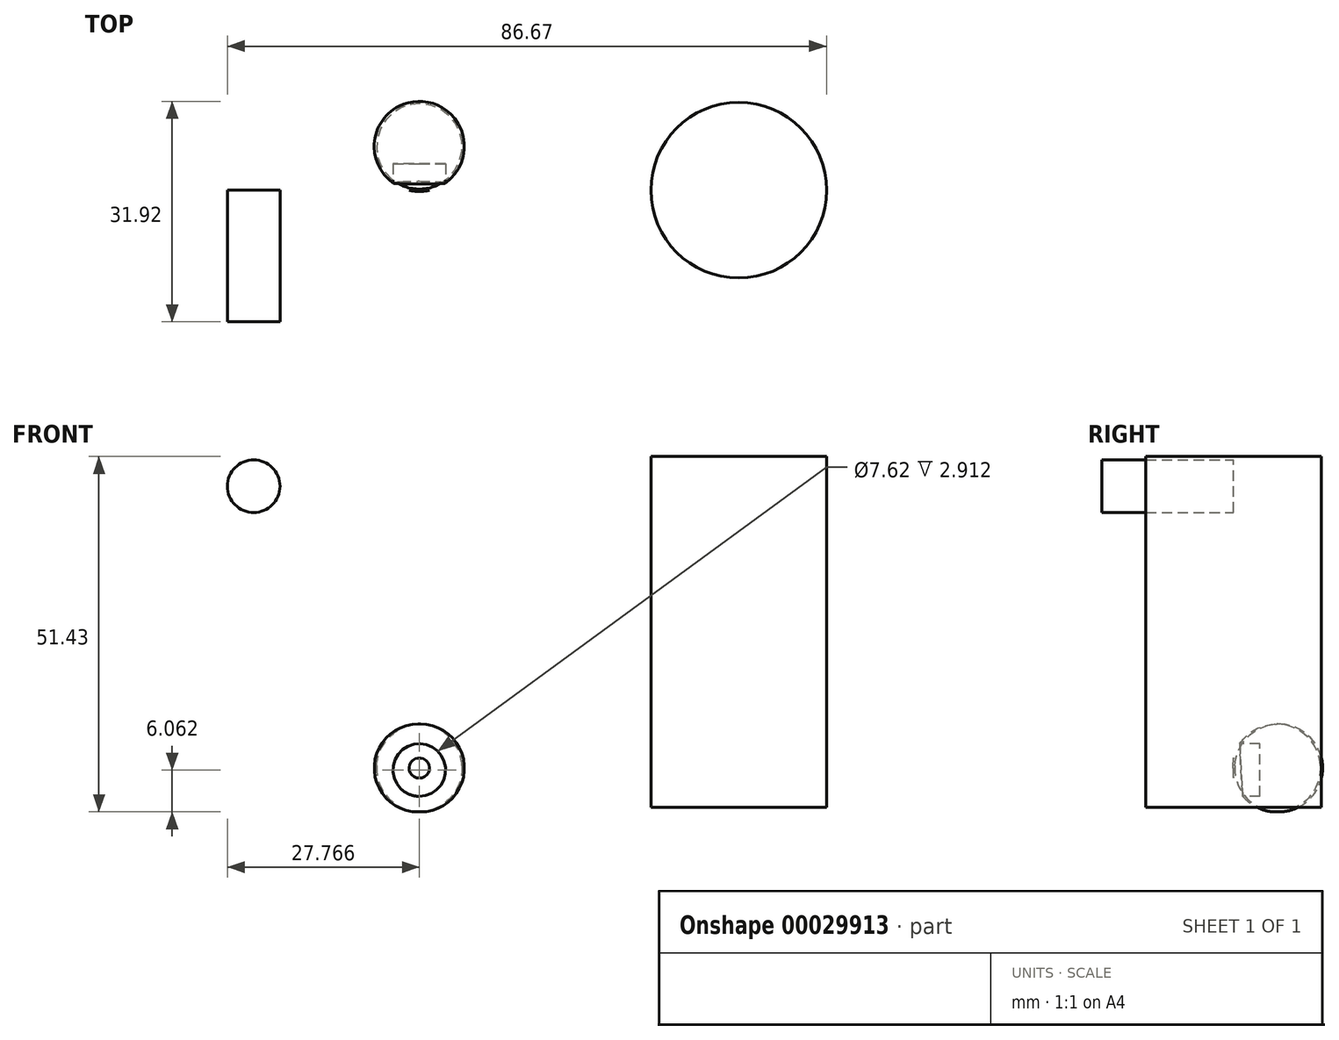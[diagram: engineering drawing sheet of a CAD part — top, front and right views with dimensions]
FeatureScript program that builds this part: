
annotation { "Feature Type Name" : "Feature", "Feature Type Description" : "" }
export const myFeature = defineFeature(function(context is Context, id is Id, definition is map)
    precondition{}
    {
        {
            var Q0;
            Q0=qCreatedBy(makeId("Front.planeOp"),FACE);
            var sketch = newSketch(context, id + "F0", { "sketchPlane" : qUnion([Q0])});
            skLineSegment(sketch, "E0", {"start": v(-25.81, -11.2) * mm, "end": v(-25.81, -23.9) * mm});
            skArc(sketch, "E1", {"start": v(-25.81, -11.2) * mm, "mid": v(-32.33, -17.54) * mm, "end": v(-25.81, -23.9) * mm});
            skSolve(sketch);
        }
        {
            var Q0;
            Q0=makeQuery(id+"F0.imprint","IMPRINT",FACE,{"disambiguationData":[TD([[makeQuery(id+"F0.imprint","IMPRINT",EDGE,{"derivedFrom":sQuery(id+"F0.wireOp",EDGE,"E0")}),-1.0]])]});
            var Q1;
            Q1=sQuery(id+"F0.wireOp",EDGE,"E0");
            revolve(context, id + "F1", {"entities" : qUnion([Q0]), "axis" : qUnion([Q1]), "revolveType" : RevolveType.FULL});
        }
        {
            var Q0;
            Q0=qCreatedBy(makeId("Front.planeOp"),FACE);
            cPlane(context, id + "F2", {"entities" : qUnion([Q0]), "cplaneType" : CPlaneType.OFFSET, "offset" : 6.35 * mm, "width" : 152.4 * mm, "height" : 152.4 * mm});
        }
        {
            var Q0;
            Q0=qCreatedBy(id+"F2.planeOp",FACE);
            var sketch = newSketch(context, id + "F3", { "sketchPlane" : qUnion([Q0])});
            skCircle(sketch, "E2", {"center": v(-25.81, -17.83) * mm, "radius": 3.8 * mm});
            skSolve(sketch);
        }
        {
            var Q0;
            Q0=makeQuery(id+"F3.imprint","IMPRINT",FACE,{"disambiguationData":[TD([[makeQuery(id+"F3.imprint","IMPRINT",EDGE,{"derivedFrom":sQuery(id+"F3.wireOp",EDGE,"E2")}),1.0]])]});
            extrude(context, id + "F4", {"entities" : qUnion([Q0]), "operationType" : NewBodyOperationType.REMOVE, "oppositeDirection" : true, "depth" : 3.8 * mm});
        }
        {
            var Q0;
            Q0=qCreatedBy(id+"F2.planeOp",FACE);
            var sketch = newSketch(context, id + "F5", { "sketchPlane" : qUnion([Q0])});
            skCircle(sketch, "E3", {"center": v(-49.77, 23.25) * mm, "radius": 3.81 * mm});
            skSolve(sketch);
        }
        {
            var Q0;
            Q0=makeQuery(id+"F5.imprint","IMPRINT",FACE,{"disambiguationData":[TD([[makeQuery(id+"F5.imprint","IMPRINT",EDGE,{"derivedFrom":sQuery(id+"F5.wireOp",EDGE,"E3")}),1.0]])]});
            extrude(context, id + "F6", {"entities" : qUnion([Q0]), "depth" : 19.05 * mm});
        }
        {
            var Q0;
            Q0=qCreatedBy(id+"F2.planeOp",FACE);
            var sketch = newSketch(context, id + "F7", { "sketchPlane" : qUnion([Q0])});
            skLineSegment(sketch, "E4.bottom", {"start": v(20.4, 27.54) * mm, "end": v(33.1, 27.54) * mm});
            skLineSegment(sketch, "E4.top", {"start": v(20.4, -23.26) * mm, "end": v(33.1, -23.26) * mm});
            skLineSegment(sketch, "E4.left", {"start": v(20.4, 27.54) * mm, "end": v(20.4, -23.26) * mm});
            skLineSegment(sketch, "E4.right", {"start": v(33.1, 27.54) * mm, "end": v(33.1, -23.26) * mm});
            skSolve(sketch);
        }
        {
            var Q0;
            Q0=makeQuery(id+"F7.imprint","IMPRINT",FACE,{"disambiguationData":[TD([[makeQuery(id+"F7.imprint","IMPRINT",EDGE,{"derivedFrom":sQuery(id+"F7.wireOp",EDGE,"E4.bottom")}),-1.0]])]});
            var Q1;
            Q1=sQuery(id+"F7.wireOp",EDGE,"E4.left");
            revolve(context, id + "F8", {"entities" : qUnion([Q0]), "axis" : qUnion([Q1]), "revolveType" : RevolveType.FULL});
        }
    });
